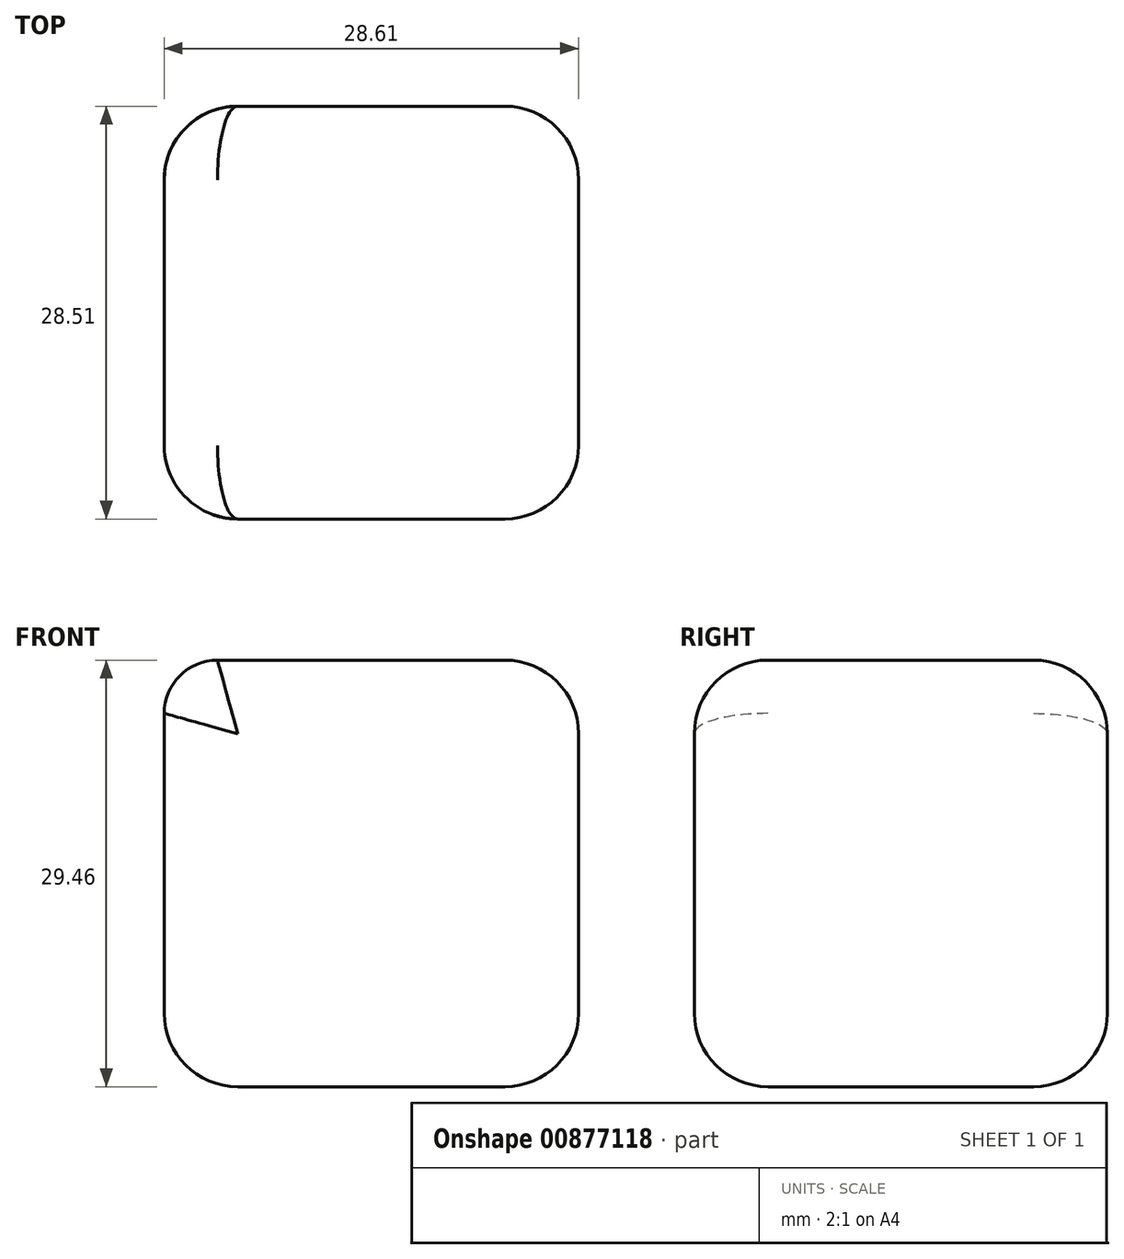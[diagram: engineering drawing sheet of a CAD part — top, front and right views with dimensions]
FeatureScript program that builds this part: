
annotation { "Feature Type Name" : "Feature", "Feature Type Description" : "" }
export const myFeature = defineFeature(function(context is Context, id is Id, definition is map)
    precondition{}
    {
        {
            var Q0;
            Q0=qCreatedBy(makeId("Top.planeOp"),FACE);
            var sketch = newSketch(context, id + "F0", { "sketchPlane" : qUnion([Q0])});
            skLineSegment(sketch, "E0", {"start": v(0, 20.88) * mm, "end": v(28.61, 20.88) * mm});
            skLineSegment(sketch, "E1", {"start": v(28.61, 20.88) * mm, "end": v(28.61, -7.63) * mm});
            skLineSegment(sketch, "E2", {"start": v(28.61, -7.63) * mm, "end": v(0, -7.63) * mm});
            skLineSegment(sketch, "E3", {"start": v(0, -7.63) * mm, "end": v(0, 20.88) * mm});
            skSolve(sketch);
        }
        {
            var Q0;
            Q0 = qSketchRegion(id + "F0", true);
            extrude(context, id + "F1", {"entities" : qUnion([Q0]), "depth" : 29.46 * mm, "offsetDistance" : 25.4 * mm});
        }
        {
            var Q0;
            Q0=makeQuery(id+"F1.opExtrude","CAP_EDGE",EDGE,{"disambiguationData":[OSD([sQuery(id+"F0.wireOp",EDGE,"E3")])],"isStart":false});
            fillet(context, id + "F2", {"entities" : qUnion([Q0]), "radius" : 3.68 * mm, "tangentPropagation" : true, "allowEdgeOverflow" : false});
        }
        {
            var Q0;
            Q0=makeQuery(id+"F1.opExtrude","SWEPT_EDGE",EDGE,{"disambiguationData":[OSD([sQuery(id+"F0.wireOp",EDGE,"E1"),sQuery(id+"F0.wireOp",EDGE,"E2")])]});
            var Q1;
            Q1=makeQuery(id+"F1.opExtrude","CAP_EDGE",EDGE,{"disambiguationData":[OSD([sQuery(id+"F0.wireOp",EDGE,"E2")])],"isStart":false});
            var Q2;
            Q2=makeQuery(id+"F1.opExtrude","CAP_EDGE",EDGE,{"disambiguationData":[OSD([sQuery(id+"F0.wireOp",EDGE,"E0")])],"isStart":false});
            var Q3;
            Q3=makeQuery(id+"F1.opExtrude","CAP_EDGE",EDGE,{"disambiguationData":[OSD([sQuery(id+"F0.wireOp",EDGE,"E1")])],"isStart":false});
            var Q4;
            Q4=makeQuery(id+"F1.opExtrude","SWEPT_EDGE",EDGE,{"disambiguationData":[OSD([sQuery(id+"F0.wireOp",EDGE,"E0"),sQuery(id+"F0.wireOp",EDGE,"E1")])]});
            var Q5;
            Q5=makeQuery(id+"F1.opExtrude","CAP_EDGE",EDGE,{"disambiguationData":[OSD([sQuery(id+"F0.wireOp",EDGE,"E2")])],"isStart":true});
            var Q6;
            Q6=makeQuery(id+"F1.opExtrude","CAP_EDGE",EDGE,{"disambiguationData":[OSD([sQuery(id+"F0.wireOp",EDGE,"E3")])],"isStart":true});
            var Q7;
            Q7=makeQuery(id+"F1.opExtrude","CAP_EDGE",EDGE,{"disambiguationData":[OSD([sQuery(id+"F0.wireOp",EDGE,"E0")])],"isStart":true});
            var Q8;
            Q8=makeQuery(id+"F1.opExtrude","CAP_EDGE",EDGE,{"disambiguationData":[OSD([sQuery(id+"F0.wireOp",EDGE,"E1")])],"isStart":true});
            fillet(context, id + "F3", {"entities" : qUnion([Q0, Q1, Q2, Q3, Q4, Q5, Q6, Q7, Q8]), "radius" : 5.08 * mm, "tangentPropagation" : true, "allowEdgeOverflow" : false});
        }
    });
